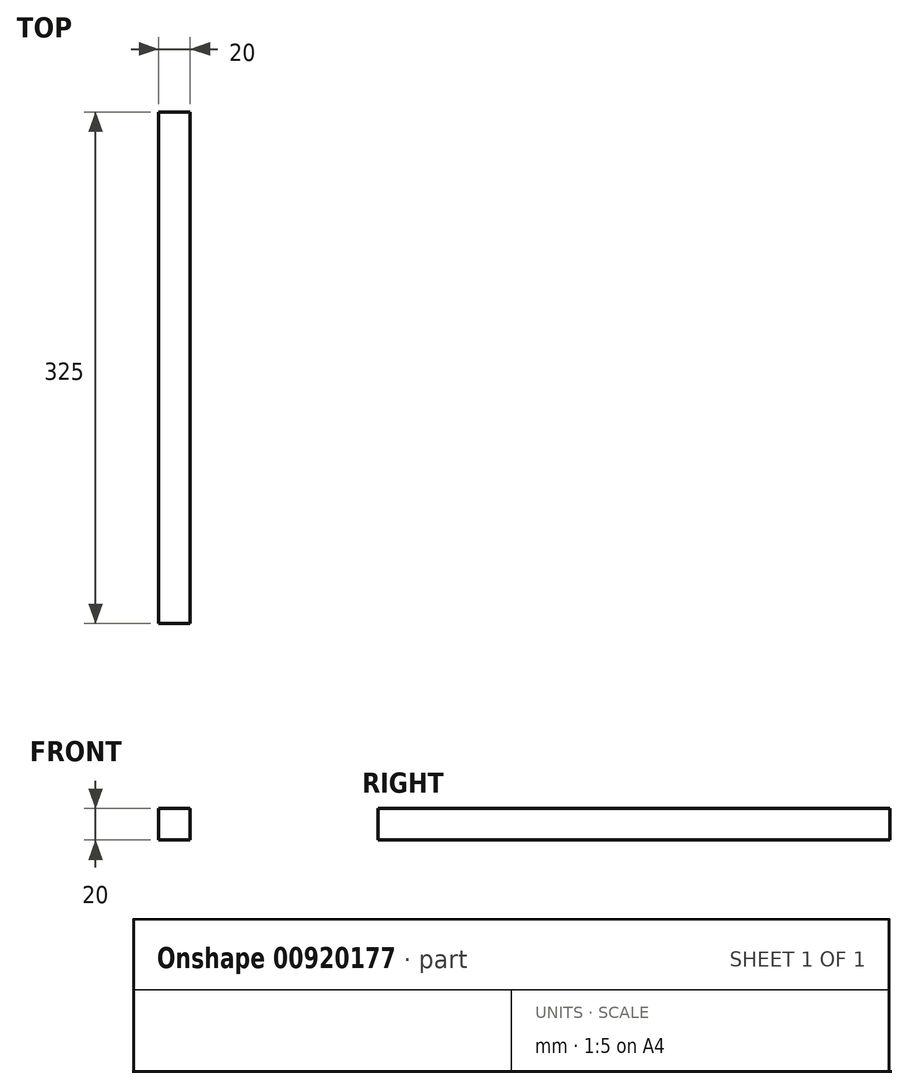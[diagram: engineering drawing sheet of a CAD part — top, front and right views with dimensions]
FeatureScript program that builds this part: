
annotation { "Feature Type Name" : "Feature", "Feature Type Description" : "" }
export const myFeature = defineFeature(function(context is Context, id is Id, definition is map)
    precondition{}
    {
        {
            var Q0;
            Q0=qCreatedBy(makeId("Front.planeOp"),FACE);
            var sketch = newSketch(context, id + "F0", { "sketchPlane" : qUnion([Q0])});
            skLineSegment(sketch, "E0.bottom", {"start": v(-1.9, 12.82) * mm, "end": v(18.1, 12.82) * mm});
            skLineSegment(sketch, "E0.top", {"start": v(-1.9, -7.18) * mm, "end": v(18.1, -7.18) * mm});
            skLineSegment(sketch, "E0.left", {"start": v(-1.9, 12.82) * mm, "end": v(-1.9, -7.18) * mm});
            skLineSegment(sketch, "E0.right", {"start": v(18.1, 12.82) * mm, "end": v(18.1, -7.18) * mm});
            skSolve(sketch);
        }
        {
            var Q0;
            Q0=qSketchRegion(id+"F0",true);
            extrude(context, id + "F1", {"entities" : qUnion([Q0]), "depth" : 325 * mm, "offsetDistance" : 25 * mm});
        }
    });
